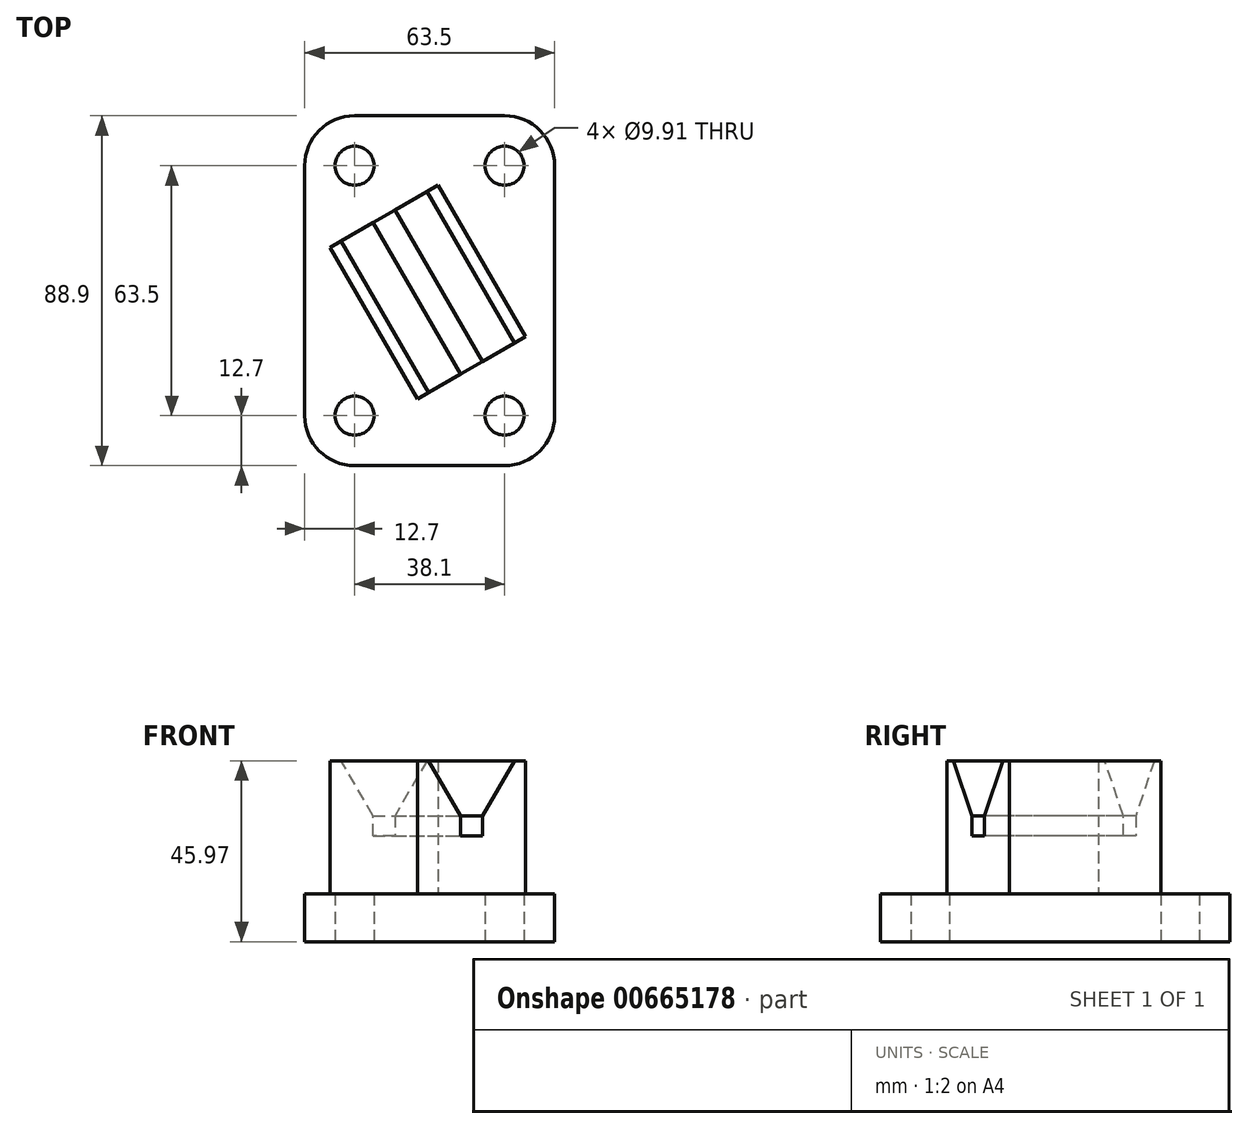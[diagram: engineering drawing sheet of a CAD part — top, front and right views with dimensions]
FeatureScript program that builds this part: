
annotation { "Feature Type Name" : "Feature", "Feature Type Description" : "" }
export const myFeature = defineFeature(function(context is Context, id is Id, definition is map)
    precondition{}
    {
        {
            var Q0;
            Q0=qCreatedBy(makeId("Top.planeOp"),FACE);
            var sketch = newSketch(context, id + "F0", { "sketchPlane" : qUnion([Q0])});
            skLineSegment(sketch, "E0", {"start": v(12.7, 0) * mm, "end": v(50.8, 0) * mm});
            skLineSegment(sketch, "E1", {"start": v(63.5, 12.7) * mm, "end": v(63.5, 76.2) * mm});
            skLineSegment(sketch, "E2", {"start": v(50.8, 88.9) * mm, "end": v(12.7, 88.9) * mm});
            skLineSegment(sketch, "E3", {"start": v(0, 76.2) * mm, "end": v(0, 12.7) * mm});
            skPoint(sketch, "E4.visualSharp", {"position": v(0, 88.9) * mm});
            skArc(sketch, "E4.filletArc", {"start": v(12.7, 88.9) * mm, "mid": v(3.72, 85.18) * mm, "end": v(0, 76.2) * mm});
            skPoint(sketch, "E5.visualSharp", {"position": v(63.5, 88.9) * mm});
            skArc(sketch, "E5.filletArc", {"start": v(63.5, 76.2) * mm, "mid": v(59.78, 85.18) * mm, "end": v(50.8, 88.9) * mm});
            skPoint(sketch, "E6.visualSharp", {"position": v(63.5, 0) * mm});
            skArc(sketch, "E6.filletArc", {"start": v(50.8, 0) * mm, "mid": v(59.78, 3.72) * mm, "end": v(63.5, 12.7) * mm});
            skPoint(sketch, "E7.visualSharp", {"position": v(0, 0) * mm});
            skArc(sketch, "E7.filletArc", {"start": v(0, 12.7) * mm, "mid": v(3.72, 3.72) * mm, "end": v(12.7, 0) * mm});
            skCircle(sketch, "E8", {"center": v(12.7, 76.2) * mm, "radius": 4.95 * mm});
            skCircle(sketch, "E9", {"center": v(50.8, 76.2) * mm, "radius": 4.95 * mm});
            skCircle(sketch, "E10", {"center": v(50.8, 12.7) * mm, "radius": 4.95 * mm});
            skCircle(sketch, "E11", {"center": v(12.7, 12.7) * mm, "radius": 4.95 * mm});
            skSolve(sketch);
        }
        {
            var Q0;
            Q0=makeQuery(id+"F0.imprint","IMPRINT",FACE,{"disambiguationData":[TD([[makeQuery(id+"F0.imprint","IMPRINT",EDGE,{"derivedFrom":sQuery(id+"F0.wireOp",EDGE,"E0")}),1.0]])]});
            extrude(context, id + "F1", {"entities" : qUnion([Q0]), "depth" : 12.2 * mm, "offsetDistance" : 25.4 * mm});
        }
        {
            var Q0;
            Q0=makeQuery(id+"F1.opExtrude","CAP_FACE",FACE,{"disambiguationData":[OSD([sQuery(id+"F0.wireOp",EDGE,"E0"),sQuery(id+"F0.wireOp",EDGE,"E1"),sQuery(id+"F0.wireOp",EDGE,"E2"),sQuery(id+"F0.wireOp",EDGE,"E3"),sQuery(id+"F0.wireOp",EDGE,"E4.filletArc"),sQuery(id+"F0.wireOp",EDGE,"E5.filletArc"),sQuery(id+"F0.wireOp",EDGE,"E6.filletArc"),sQuery(id+"F0.wireOp",EDGE,"E7.filletArc"),sQuery(id+"F0.wireOp",EDGE,"E8"),sQuery(id+"F0.wireOp",EDGE,"E9"),sQuery(id+"F0.wireOp",EDGE,"E10"),sQuery(id+"F0.wireOp",EDGE,"E11")])],"isStart":false});
            var sketch = newSketch(context, id + "F2", { "sketchPlane" : qUnion([Q0])});
            skLineSegment(sketch, "E12", {"start": v(56.13, 32.77) * mm, "end": v(28.64, 16.9) * mm});
            skLineSegment(sketch, "E13", {"start": v(28.64, 16.9) * mm, "end": v(6.41, 55.39) * mm});
            skLineSegment(sketch, "E14", {"start": v(6.41, 55.39) * mm, "end": v(33.9, 71.26) * mm});
            skLineSegment(sketch, "E15", {"start": v(33.9, 71.26) * mm, "end": v(56.13, 32.77) * mm});
            skSolve(sketch);
        }
        {
            var Q0;
            Q0=makeQuery(id+"F2.imprint","IMPRINT",FACE,{"disambiguationData":[TD([[makeQuery(id+"F2.imprint","IMPRINT",EDGE,{"derivedFrom":sQuery(id+"F2.wireOp",EDGE,"E12")}),-1.0]])]});
            extrude(context, id + "F3", {"entities" : qUnion([Q0]), "operationType" : NewBodyOperationType.ADD, "depth" : 33.78 * mm, "offsetDistance" : 25.4 * mm});
        }
        {
            var Q0;
            Q0=makeQuery(id+"F3.opExtrude","SWEPT_FACE",FACE,{"disambiguationData":[OSD([sQuery(id+"F2.wireOp",EDGE,"E12")])]});
            var sketch = newSketch(context, id + "F4", { "sketchPlane" : qUnion([Q0])});
            skLineSegment(sketch, "E16.0", {"start": v(65, 45.97) * mm, "end": v(33.25, 45.97) * mm});
            skLineSegment(sketch, "E17", {"start": v(36.55, 45.97) * mm, "end": v(45.95, 32) * mm});
            skLineSegment(sketch, "E18", {"start": v(45.95, 32) * mm, "end": v(45.95, 26.92) * mm});
            skLineSegment(sketch, "E19", {"start": v(45.95, 26.92) * mm, "end": v(52.3, 26.92) * mm});
            skLineSegment(sketch, "E20", {"start": v(52.3, 26.92) * mm, "end": v(52.3, 32) * mm});
            skLineSegment(sketch, "E21", {"start": v(52.3, 32) * mm, "end": v(61.7, 45.97) * mm});
            skLineSegment(sketch, "E22", {"start": v(49.12, 45.97) * mm, "end": v(49.12, 26.92) * mm, "construction": true});
            skSolve(sketch);
        }
        {
            var Q0;
            {var subQ0=sQuery(id+"F4.wireOp",EDGE,"E17");Q0=makeQuery(id+"F4.imprint","IMPRINT",FACE,{"disambiguationData":[TD([[makeQuery(id+"F4.imprint","IMPRINT",EDGE,{"derivedFrom":subQ0}),1.0]])]});}
            extrude(context, id + "F5", {"entities" : qUnion([Q0]), "operationType" : NewBodyOperationType.REMOVE, "endBound" : BoundingType.THROUGH_ALL, "oppositeDirection" : true, "depth" : 25.4 * mm, "offsetDistance" : 25.4 * mm});
        }
    });
